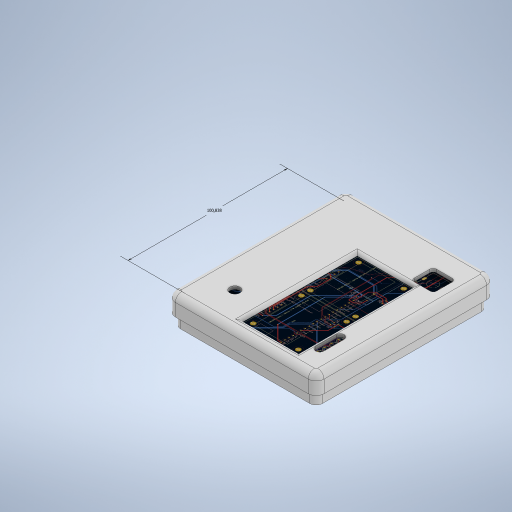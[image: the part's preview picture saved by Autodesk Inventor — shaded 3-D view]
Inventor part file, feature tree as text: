
AUTODESK INVENTOR PART (.ipt)
format: ipt  version: 2024.4 (Build 284460000, 460)  size: 844,288 bytes
history: native  units: mm
features: fillet x7, sketch x5, extrude x4, other x1
ambient origin geometry x8: Origin, YZ Plane, XZ Plane, XY Plane, X Axis, Y Axis, Z Axis, Center Point
bodies: Solid1 (feature_tree)
feature tree (17):
  sketch  "Sketch1"  dims[d3=100.838mm d8=2.15mm]
  extrude  "Extrusion1"  Depth=2.15mm
  extrude  "Extrusion2"  Depth=3.85mm
  extrude  "Extrusion3"  Depth=10.0mm TaperAngle=0.0deg
  fillet  "Fillet3"  Radius=2.0mm
  fillet  "Fillet4"  Radius=2.0mm
  fillet  "Fillet5"  Radius=4.0mm
  extrude  "Extrusion4"  Depth=2.0mm
  fillet  "Fillet6"  Radius=2.0mm
  fillet  "Fillet7"  Radius=2.0mm
  fillet  "Fillet8"  Radius=4.0mm
  fillet  "Fillet9"  Radius=4.0mm
  other  "Image1"
  sketch  "Sketch2"  dims[d9=3.85mm d10=3.85mm]
  sketch  "Sketch3"  dims[d11=2.15mm d12=10.0mm d13=0.0mm d14=2.0mm d15=0.0mm d16=2.0mm d17=0.0mm d20=4.0mm]
  sketch  "Sketch4"  dims[d22=2.6mm d23=2.0mm d24=2.0mm d25=2.0mm]
  sketch  "Sketch6"  dims[d26=7.0mm d27=10.0mm d28=0.0mm d29=0.0mm d30=4.0mm d31=4.0mm d32=2.0mm d33=5.0mm d34=6.5mm d39=94.030423mm d40=112.838mm d35=0.0mm d36=0.0mm]
